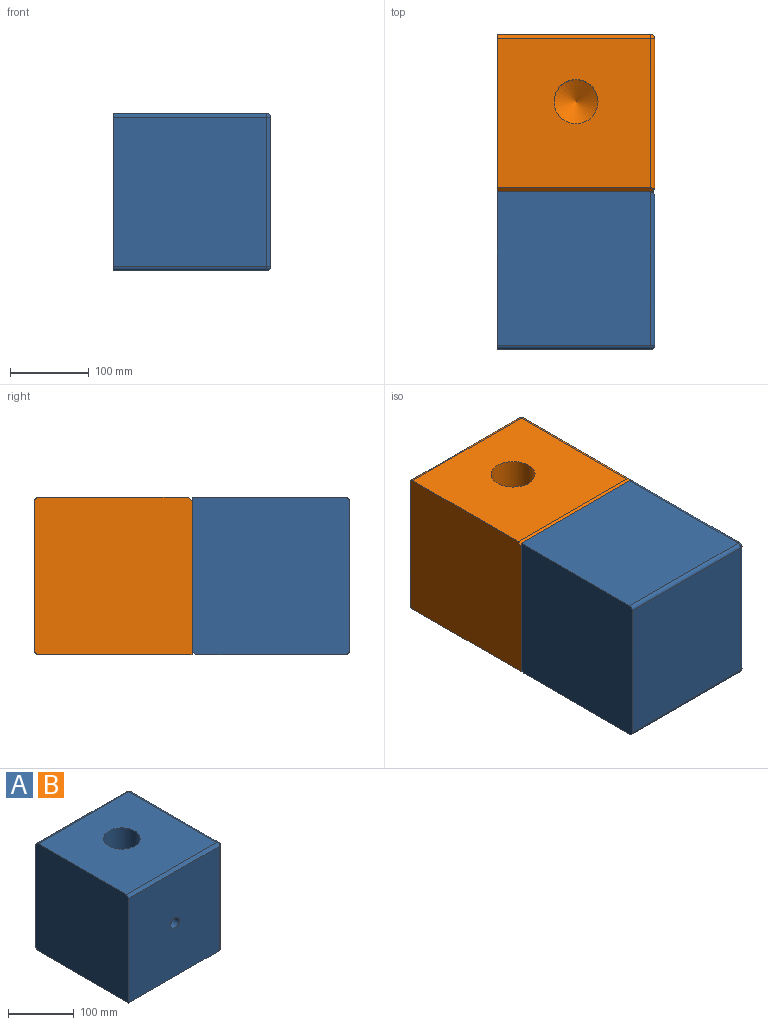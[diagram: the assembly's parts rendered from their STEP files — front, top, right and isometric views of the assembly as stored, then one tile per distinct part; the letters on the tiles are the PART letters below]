
ASSEMBLY  parts=2 mates=1
PART A: 19 faces, bbox 200x200x200 mm
  f0: plane 195x190mm, normal (0,0,1), area 34587mm2, adj f1,f8,f9,f14,f18
  f1: plane 200x200mm, normal (-1,0,0), area 39976.8mm2, adj f0,f2,f4,f5,f8,f14,f15
  f2: plane 195x195mm, normal (0,0,-1), area 38025mm2, adj f1,f4,f11,f15
  f3: plane 190x190mm, normal (1,0,0), area 36100mm2, adj f9,f10,f11,f12
  f4: plane 195x195mm, normal (0,-1,0), area 37756.2mm2, adj f1,f2,f7,f8,f10
  f5: plane 195x190mm, normal (0,1,0), area 37050mm2, adj f1,f12,f14,f15
  f6: cone r=0mm half-angle=59deg, axis (0,-1,0), area 313.6mm2, adj f7
  f7: cylinder r=9.25mm len=22.5mm, axis (0,-1,0), area 1307.7mm2, adj f4,f6
  f8: plane 199.33x5mm, normal (0,-0.71,0.71), area 1400.6mm2, adj f0,f1,f4,f9,f10
  f9: cylinder r=5mm len=192.5mm, axis (0,1,0), area 1500.1mm2, adj f0,f3,f8,f10,f13
  f10: cylinder r=5mm len=197.5mm, axis (0,0,-1), area 1525.1mm2, adj f3,f4,f8,f9,f11
  f11: cylinder r=5mm len=195mm, axis (0,-1,0), area 1517.3mm2, adj f2,f3,f10,f16
  f12: cylinder r=5mm len=190mm, axis (0,0,1), area 1492.3mm2, adj f3,f5,f13,f16
  f13: sphere r=5mm, area 39.3mm2, adj f9,f12,f14
  f14: cylinder r=5mm len=195mm, axis (-1,0,0), area 1531.5mm2, adj f0,f1,f5,f13
  f15: cylinder r=5mm len=195mm, axis (1,0,0), area 1531.5mm2, adj f1,f2,f5,f16
  f16: sphere r=5mm, area 39.3mm2, adj f11,f12,f15
  f17: cone r=0mm half-angle=59deg, axis (0,0,1), area 2873.4mm2, adj f18
  f18: cylinder r=28mm len=72mm, axis (0,0,1), area 12666.9mm2, adj f0,f17
PART B: same geometry as A
PLACE A rot(axis=(1,0,0),180deg) t=(-61.28,-213.46,32.87)mm
PLACE B t=(-61.28,-13.46,32.87)mm
MATE parallel A.f6 <-> B.f6  axis (0,1,0) through (-61.28,-113.46,32.87)mm
